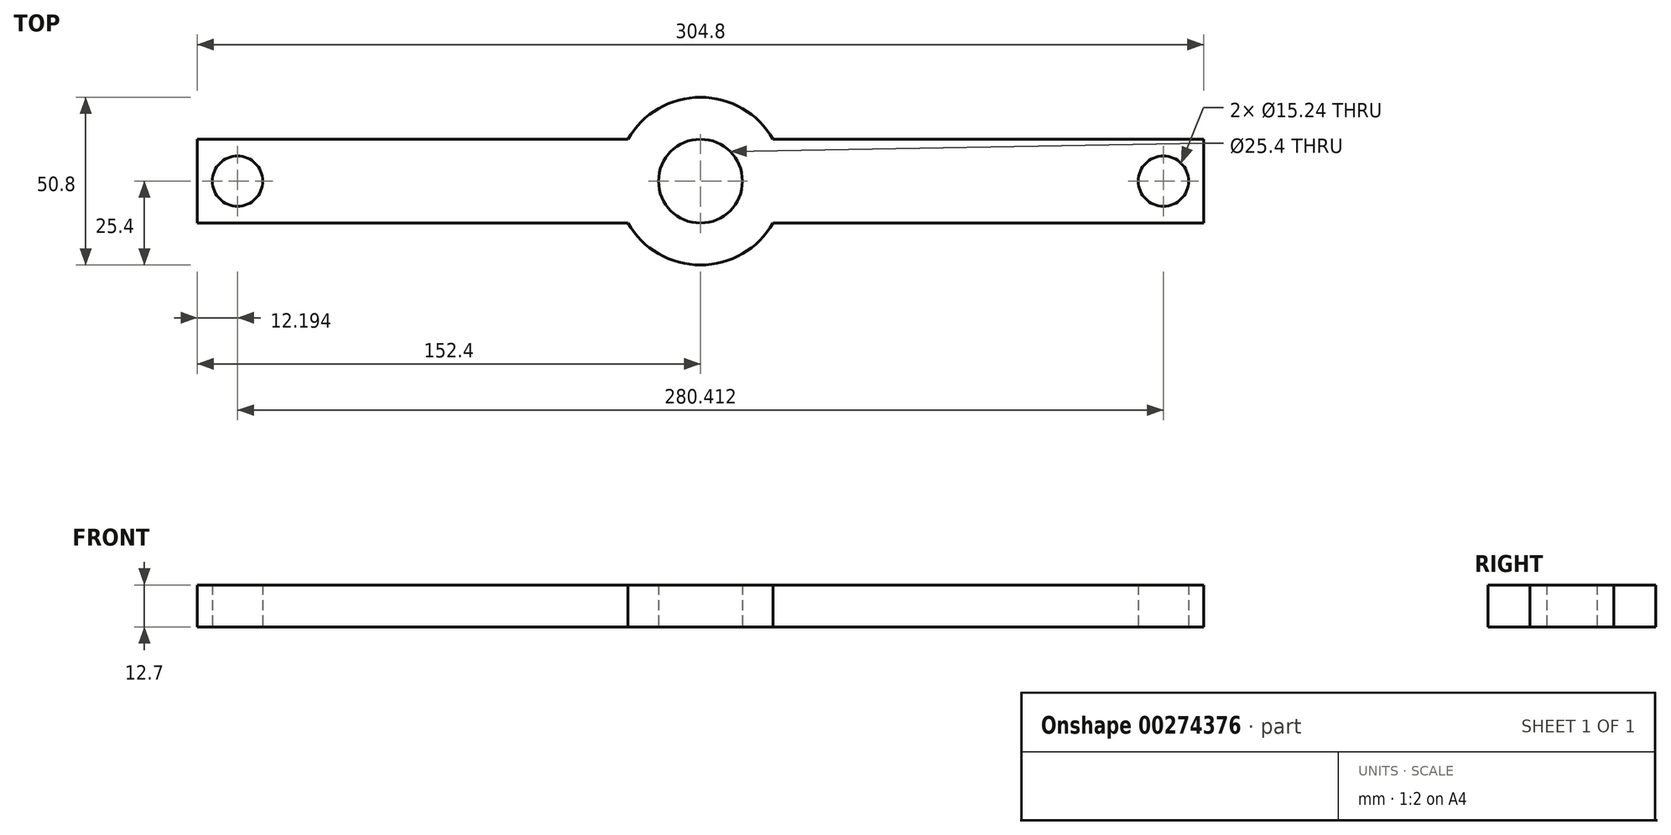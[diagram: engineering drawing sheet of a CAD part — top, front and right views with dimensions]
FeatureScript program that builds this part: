
annotation { "Feature Type Name" : "Feature", "Feature Type Description" : "" }
export const myFeature = defineFeature(function(context is Context, id is Id, definition is map)
    precondition{}
    {
        {
            var Q0;
            Q0=qCreatedBy(makeId("Top.planeOp"),FACE);
            var sketch = newSketch(context, id + "F0", { "sketchPlane" : qUnion([Q0])});
            skArc(sketch, "E0", {"start": v(22, 12.7) * mm, "mid": v(0, 25.4) * mm, "end": v(-22, 12.7) * mm});
            skLineSegment(sketch, "E1.top", {"start": v(22, -12.7) * mm, "end": v(152.4, -12.7) * mm});
            skLineSegment(sketch, "E1.right", {"start": v(152.4, 0) * mm, "end": v(152.4, -12.7) * mm});
            skLineSegment(sketch, "E2.top", {"start": v(22, 12.7) * mm, "end": v(152.4, 12.7) * mm});
            skLineSegment(sketch, "E2.right", {"start": v(152.4, 0) * mm, "end": v(152.4, 12.7) * mm});
            skLineSegment(sketch, "E3.top", {"start": v(-22, 12.7) * mm, "end": v(-152.4, 12.7) * mm});
            skLineSegment(sketch, "E3.right", {"start": v(-152.4, 0) * mm, "end": v(-152.4, 12.7) * mm});
            skLineSegment(sketch, "E4.bottom", {"start": v(-22, -12.7) * mm, "end": v(-152.4, -12.7) * mm});
            skLineSegment(sketch, "E4.right", {"start": v(-152.4, -12.7) * mm, "end": v(-152.4, 0) * mm});
            skCircle(sketch, "E5", {"center": v(-140.2, 0) * mm, "radius": 7.62 * mm});
            skLineSegment(sketch, "E6", {"start": v(-140.2, 6.35) * mm, "end": v(-140.2, 7.62) * mm});
            skLineSegment(sketch, "E7", {"start": v(140.2, 6.35) * mm, "end": v(140.2, 7.62) * mm});
            skCircle(sketch, "E8", {"center": v(140.2, 0) * mm, "radius": 7.62 * mm});
            skPoint(sketch, "E9.orphan", {"position": v(140.2, 12.7) * mm});
            skPoint(sketch, "E10.orphan", {"position": v(152.4, 6.35) * mm});
            skPoint(sketch, "E11.orphan", {"position": v(-152.4, 6.35) * mm});
            skPoint(sketch, "E12.orphan", {"position": v(-140.2, 12.7) * mm});
            skCircle(sketch, "E13", {"center": v(0, 0) * mm, "radius": 12.7 * mm});
            skArc(sketch, "E14.trimOffspring", {"start": v(-22, -12.7) * mm, "mid": v(0, -25.4) * mm, "end": v(22, -12.7) * mm});
            skSolve(sketch);
        }
        {
            var Q0;
            Q0=makeQuery(id+"F0.imprint","IMPRINT",FACE,{"disambiguationData":[TD([[makeQuery(id+"F0.imprint","IMPRINT",EDGE,{"derivedFrom":sQuery(id+"F0.wireOp",EDGE,"E0")}),1.0]])]});
            extrude(context, id + "F1", {"entities" : qUnion([Q0]), "depth" : 12.7 * mm});
        }
    });
